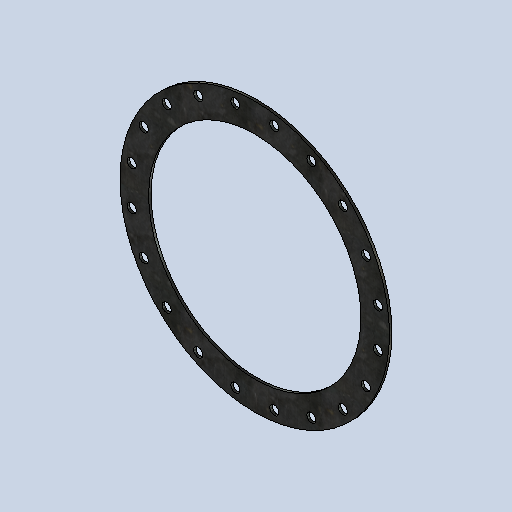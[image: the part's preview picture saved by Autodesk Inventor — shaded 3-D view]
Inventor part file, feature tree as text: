
AUTODESK INVENTOR PART (.ipt)
format: ipt  version: 2025.1 (Build 291241020, 241B)  size: 224,256 bytes
history: native  units: mm
features: sketch x2, other x2, extrude x1, pattern_circular x1, projected_geometry x1
ambient origin geometry x8: Origin, YZ Plane, XZ Plane, XY Plane, X Axis, Y Axis, Z Axis, Center Point
bodies: Solid1 (feature_tree)
feature tree (7):
  extrude  "Extrusion1"  Depth=6.0mm TaperAngle=0.0deg
  pattern_circular  "Circular Pattern1"  Count=31  [1 undecoded]
  sketch  "Sketch1"  dims[d0=512.0mm d1=670.0mm d2=6.0mm d3=0.0mm]
  sketch  "Sketch2"  dims[d4=528.0mm d5=310.0mm d7=23.0mm d8=6.0mm d9=6.0mm d10=0.0mm d11=200.0mm d12=360.0deg]
  projected_geometry  "Projected Loop1"
  other  "Cut1"
  other  "Definition1"
note: 1 required parameter value undecoded (feature->parameter linkage not recoverable at this tier; creation-order binding heuristic only, values carry confidence <= 0.55)
